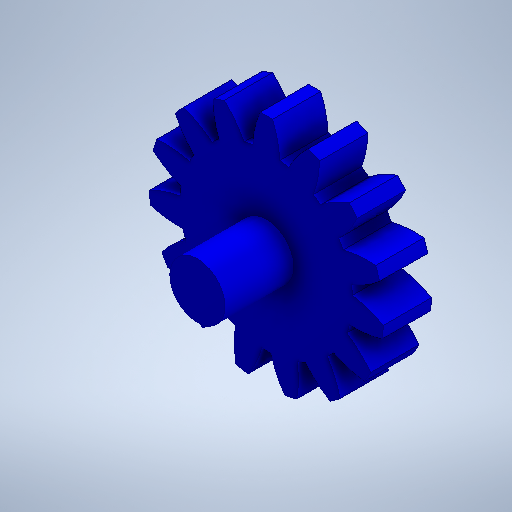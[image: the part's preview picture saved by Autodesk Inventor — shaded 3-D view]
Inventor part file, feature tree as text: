
AUTODESK INVENTOR PART (.ipt)
format: ipt  version: 2025.2 (Build 292293000, 293)  size: 378,880 bytes
history: native  units: mm (DEFAULTED — no unit token found)
features: plane x3, other x3, extrude x2, sketch x2
ambient origin geometry x8: Origin, YZ Plane, XZ Plane, XY Plane, X Axis, Y Axis, Z Axis, Center Point
bodies: Solid1 (feature_tree)
feature tree (10):
  extrude  "Extrusion1"  Depth=7.0mm TaperAngle=0.0deg
  plane  "Work Plane2"
  plane  "Work Plane8"
  plane  "Work Plane9"
  other  "Spur Gear"
  extrude  "Extrusion2"  Depth=10.0mm TaperAngle=0.0deg
  sketch  "Sketch1"  dims[d0=34.0mm d1=7.0mm d2=0.0mm]
  other  "Srf1"
  sketch  "Sketch3"  dims[d3=30.0mm d4=10.0mm d5=0.0mm d16=60.0mm d17=0.0mm d34=2.094395mm d39=0.0mm d41=0.0mm d43=60.0mm d46=60.0mm d47=0.0mm d48=0.0mm d49=8.0mm d50=10.0mm d51=0.0mm]
  other  "Pitch Diameter"
